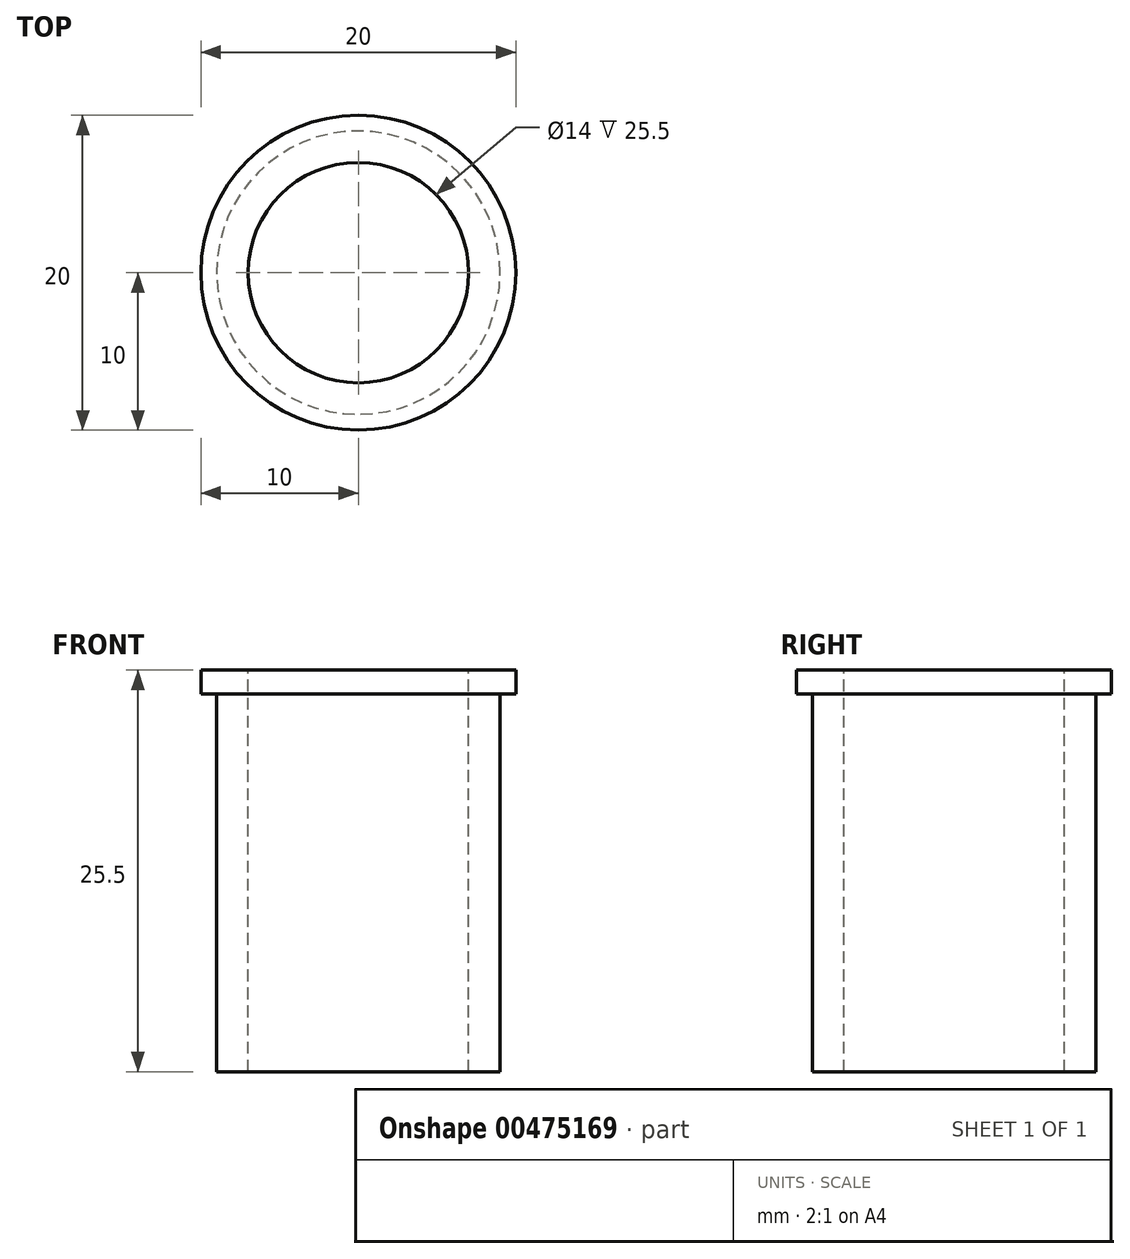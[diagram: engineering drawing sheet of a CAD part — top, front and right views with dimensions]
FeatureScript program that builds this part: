
annotation { "Feature Type Name" : "Feature", "Feature Type Description" : "" }
export const myFeature = defineFeature(function(context is Context, id is Id, definition is map)
    precondition{}
    {
        {
            var Q0;
            Q0=qCreatedBy(makeId("Top.planeOp"),FACE);
            var sketch = newSketch(context, id + "F0", { "sketchPlane" : qUnion([Q0])});
            skCircle(sketch, "E0", {"center": v(0, 0) * mm, "radius": 10 * mm});
            skSolve(sketch);
        }
        {
            var Q0;
            Q0=makeQuery(id+"F0.imprint","IMPRINT",FACE,{"disambiguationData":[TD([[makeQuery(id+"F0.imprint","IMPRINT",EDGE,{"derivedFrom":sQuery(id+"F0.wireOp",EDGE,"E0")}),1.0]])]});
            extrude(context, id + "F1", {"entities" : qUnion([Q0]), "oppositeDirection" : true, "depth" : 1.5 * mm});
        }
        {
            var Q0;
            Q0=makeQuery(id+"F1.opExtrude","CAP_FACE",FACE,{"disambiguationData":[OSD([sQuery(id+"F0.wireOp",EDGE,"E0")])],"isStart":false});
            var sketch = newSketch(context, id + "F2", { "sketchPlane" : qUnion([Q0])});
            skCircle(sketch, "E1", {"center": v(0, 0) * mm, "radius": 9 * mm});
            skSolve(sketch);
        }
        {
            var Q0;
            Q0=makeQuery(id+"F2.imprint","IMPRINT",FACE,{"disambiguationData":[TD([[makeQuery(id+"F2.imprint","IMPRINT",EDGE,{"derivedFrom":sQuery(id+"F2.wireOp",EDGE,"E1")}),1.0]])]});
            extrude(context, id + "F3", {"entities" : qUnion([Q0]), "operationType" : NewBodyOperationType.ADD, "depth" : 24 * mm});
        }
        {
            var Q0;
            Q0=makeQuery(id+"F1.opExtrude","CAP_FACE",FACE,{"disambiguationData":[OSD([sQuery(id+"F0.wireOp",EDGE,"E0")])],"isStart":true});
            var sketch = newSketch(context, id + "F4", { "sketchPlane" : qUnion([Q0])});
            skCircle(sketch, "E2", {"center": v(0, 0) * mm, "radius": 7 * mm});
            skSolve(sketch);
        }
        {
            var Q0;
            Q0=makeQuery(id+"F4.imprint","IMPRINT",FACE,{"disambiguationData":[TD([[makeQuery(id+"F4.imprint","IMPRINT",EDGE,{"derivedFrom":sQuery(id+"F4.wireOp",EDGE,"E2")}),1.0]])]});
            extrude(context, id + "F5", {"entities" : qUnion([Q0]), "operationType" : NewBodyOperationType.REMOVE, "endBound" : BoundingType.THROUGH_ALL, "oppositeDirection" : true, "depth" : 25 * mm});
        }
    });
